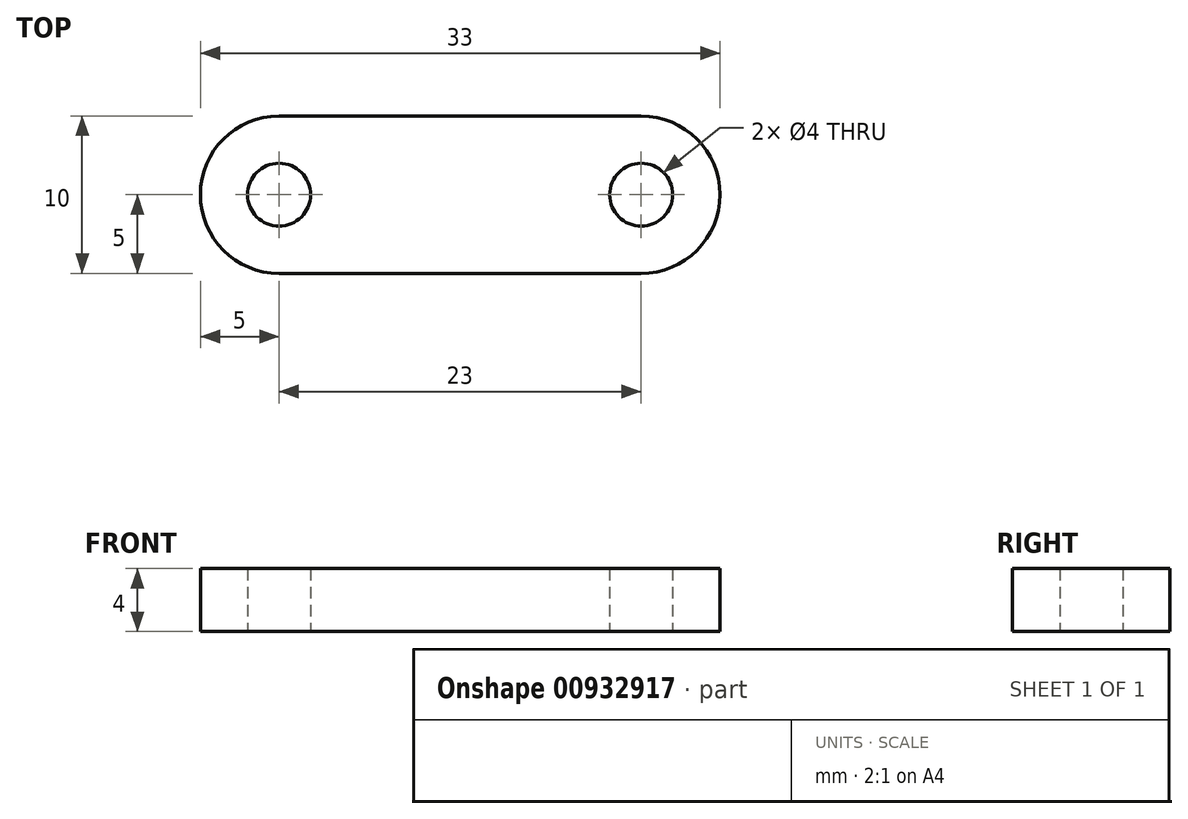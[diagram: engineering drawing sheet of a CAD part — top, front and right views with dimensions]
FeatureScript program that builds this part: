
annotation { "Feature Type Name" : "Feature", "Feature Type Description" : "" }
export const myFeature = defineFeature(function(context is Context, id is Id, definition is map)
    precondition{}
    {
        {
            var Q0;
            Q0=qCreatedBy(makeId("Top.planeOp"),FACE);
            var sketch = newSketch(context, id + "F0", { "sketchPlane" : qUnion([Q0])});
            skCircle(sketch, "E0", {"center": v(-11.5, 0) * mm, "radius": 2 * mm});
            skArc(sketch, "E1", {"start": v(-11.5, 5) * mm, "mid": v(-16.5, 0) * mm, "end": v(-11.5, -5) * mm});
            skLineSegment(sketch, "E2", {"start": v(-11.5, 6.7) * mm, "end": v(-11.5, -7.76) * mm, "construction": true});
            skLineSegment(sketch, "E3", {"start": v(-11.5, 5) * mm, "end": v(0, 5) * mm});
            skLineSegment(sketch, "E4", {"start": v(-11.5, -5) * mm, "end": v(0, -5) * mm});
            skLineSegment(sketch, "E5.MirrorCS", {"start": v(11.5, 5) * mm, "end": v(0, 5) * mm});
            skLineSegment(sketch, "E6.MirrorCS", {"start": v(11.5, -5) * mm, "end": v(0, -5) * mm});
            skArc(sketch, "E7.MirrorCS", {"start": v(11.5, 5) * mm, "mid": v(16.5, 0) * mm, "end": v(11.5, -5) * mm});
            skCircle(sketch, "E8.MirrorC", {"center": v(11.5, 0) * mm, "radius": 2 * mm});
            skSolve(sketch);
        }
        {
            var Q0;
            Q0=makeQuery(id+"F0.imprint","IMPRINT",FACE,{"disambiguationData":[TD([[makeQuery(id+"F0.imprint","IMPRINT",EDGE,{"derivedFrom":sQuery(id+"F0.wireOp",EDGE,"E0")}),-1.0]])]});
            extrude(context, id + "F1", {"entities" : qUnion([Q0]), "depth" : 4 * mm, "offsetDistance" : 25 * mm});
        }
    });
